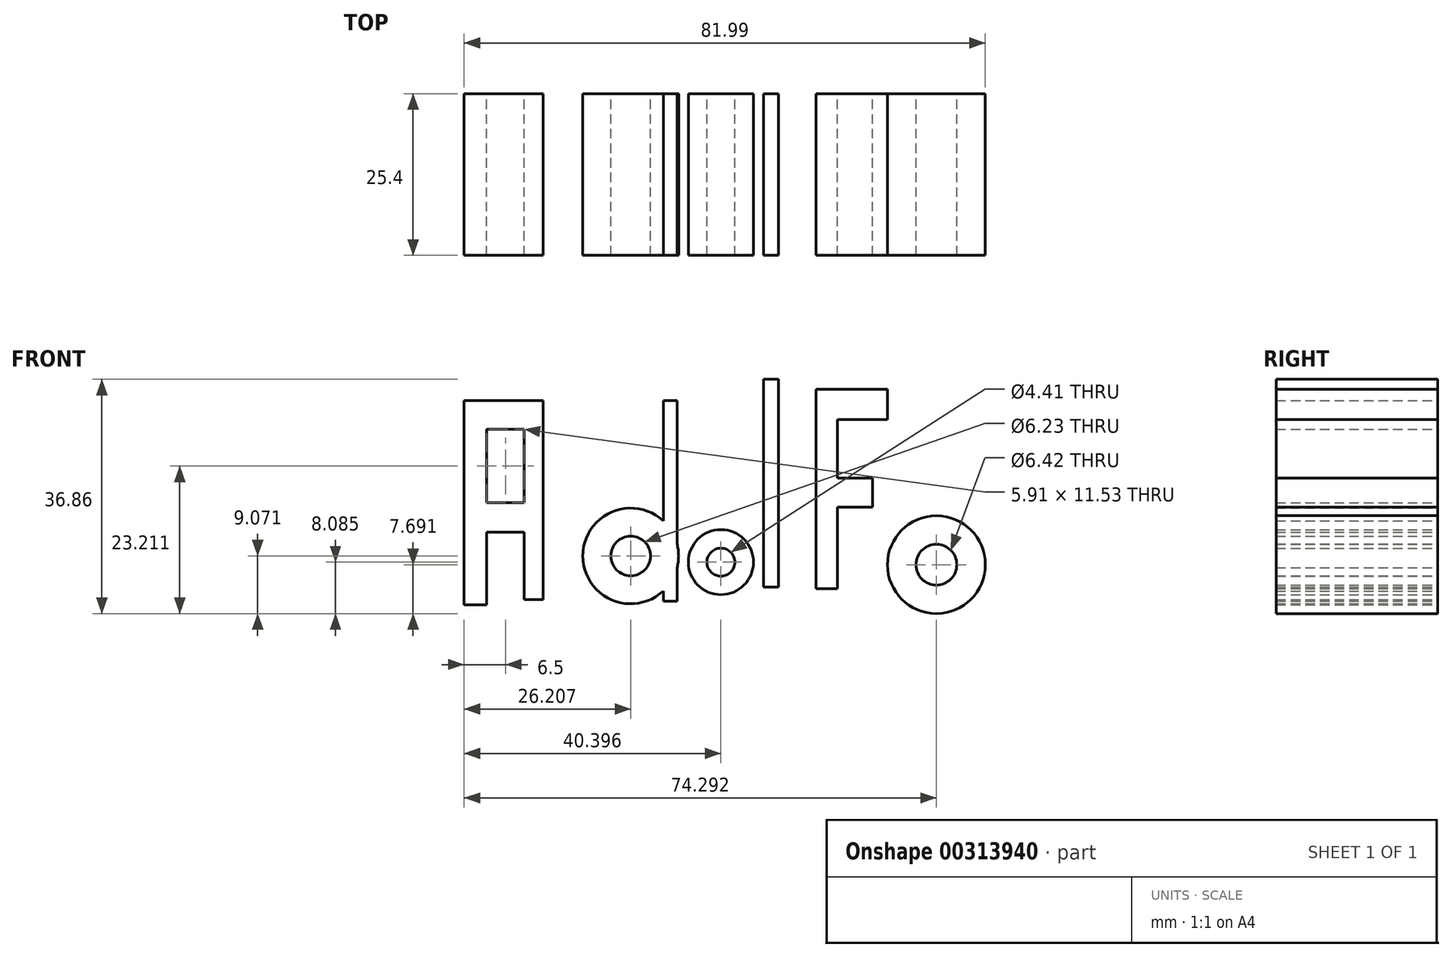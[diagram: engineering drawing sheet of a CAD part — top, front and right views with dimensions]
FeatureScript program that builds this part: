
annotation { "Feature Type Name" : "Feature", "Feature Type Description" : "" }
export const myFeature = defineFeature(function(context is Context, id is Id, definition is map)
    precondition{}
    {
        {
            var Q0;
            Q0=qCreatedBy(makeId("Front.planeOp"),FACE);
            var sketch = newSketch(context, id + "F0", { "sketchPlane" : qUnion([Q0])});
            skCircle(sketch, "E0", {"center": v(-45.52, 28.18) * mm, "radius": 7.53 * mm});
            skCircle(sketch, "E1", {"center": v(-31.33, 27.2) * mm, "radius": 5.12 * mm});
            skCircle(sketch, "E2", {"center": v(2.56, 26.8) * mm, "radius": 7.7 * mm});
            skLineSegment(sketch, "E3.bottom", {"start": v(-71.73, 20.5) * mm, "end": v(-68.19, 20.5) * mm});
            skLineSegment(sketch, "E3.top", {"start": v(-71.73, 52.62) * mm, "end": v(-68.19, 52.62) * mm});
            skLineSegment(sketch, "E3.left", {"start": v(-71.73, 20.5) * mm, "end": v(-71.73, 52.62) * mm});
            skLineSegment(sketch, "E3.right", {"start": v(-68.19, 20.5) * mm, "end": v(-68.19, 52.62) * mm});
            skLineSegment(sketch, "E4.bottom", {"start": v(-71.73, 52.62) * mm, "end": v(-59.32, 52.62) * mm});
            skLineSegment(sketch, "E4.top", {"start": v(-71.73, 48.08) * mm, "end": v(-59.32, 48.08) * mm});
            skLineSegment(sketch, "E4.left", {"start": v(-71.73, 52.62) * mm, "end": v(-71.73, 48.08) * mm});
            skLineSegment(sketch, "E4.right", {"start": v(-59.32, 52.62) * mm, "end": v(-59.32, 48.08) * mm});
            skLineSegment(sketch, "E5.bottom", {"start": v(-59.32, 52.62) * mm, "end": v(-62.27, 52.62) * mm});
            skLineSegment(sketch, "E5.top", {"start": v(-59.32, 21.28) * mm, "end": v(-62.27, 21.28) * mm});
            skLineSegment(sketch, "E5.left", {"start": v(-59.32, 52.62) * mm, "end": v(-59.32, 21.28) * mm});
            skLineSegment(sketch, "E5.right", {"start": v(-62.27, 52.62) * mm, "end": v(-62.27, 21.28) * mm});
            skLineSegment(sketch, "E6.bottom", {"start": v(-71.73, 36.56) * mm, "end": v(-59.32, 36.56) * mm});
            skLineSegment(sketch, "E6.top", {"start": v(-71.73, 31.93) * mm, "end": v(-59.32, 31.93) * mm});
            skLineSegment(sketch, "E6.left", {"start": v(-71.73, 36.56) * mm, "end": v(-71.73, 31.93) * mm});
            skLineSegment(sketch, "E6.right", {"start": v(-59.32, 36.56) * mm, "end": v(-59.32, 31.93) * mm});
            skLineSegment(sketch, "E7.bottom", {"start": v(-38.23, 21.09) * mm, "end": v(-40.4, 21.09) * mm});
            skLineSegment(sketch, "E7.top", {"start": v(-38.23, 52.62) * mm, "end": v(-40.4, 52.62) * mm});
            skLineSegment(sketch, "E7.left", {"start": v(-38.23, 21.09) * mm, "end": v(-38.23, 52.62) * mm});
            skLineSegment(sketch, "E7.right", {"start": v(-40.4, 21.09) * mm, "end": v(-40.4, 52.62) * mm});
            skLineSegment(sketch, "E8.bottom", {"start": v(-22.27, 23.25) * mm, "end": v(-24.63, 23.25) * mm});
            skLineSegment(sketch, "E8.top", {"start": v(-22.27, 55.97) * mm, "end": v(-24.63, 55.97) * mm});
            skLineSegment(sketch, "E8.left", {"start": v(-22.27, 23.25) * mm, "end": v(-22.27, 55.97) * mm});
            skLineSegment(sketch, "E8.right", {"start": v(-24.63, 23.25) * mm, "end": v(-24.63, 55.97) * mm});
            skLineSegment(sketch, "E9.bottom", {"start": v(-16.36, 54.4) * mm, "end": v(-13, 54.4) * mm});
            skLineSegment(sketch, "E9.top", {"start": v(-16.36, 23.06) * mm, "end": v(-13, 23.06) * mm});
            skLineSegment(sketch, "E9.left", {"start": v(-16.36, 54.4) * mm, "end": v(-16.36, 23.06) * mm});
            skLineSegment(sketch, "E9.right", {"start": v(-13, 54.4) * mm, "end": v(-13, 23.06) * mm});
            skLineSegment(sketch, "E10.bottom", {"start": v(-16.36, 54.4) * mm, "end": v(-5.12, 54.4) * mm});
            skLineSegment(sketch, "E10.top", {"start": v(-16.36, 49.66) * mm, "end": v(-5.12, 49.66) * mm});
            skLineSegment(sketch, "E10.left", {"start": v(-16.36, 54.4) * mm, "end": v(-16.36, 49.66) * mm});
            skLineSegment(sketch, "E10.right", {"start": v(-5.12, 54.4) * mm, "end": v(-5.12, 49.66) * mm});
            skLineSegment(sketch, "E11.bottom", {"start": v(-16.36, 40.4) * mm, "end": v(-7.49, 40.4) * mm});
            skLineSegment(sketch, "E11.top", {"start": v(-16.36, 35.87) * mm, "end": v(-7.49, 35.87) * mm});
            skLineSegment(sketch, "E11.left", {"start": v(-16.36, 40.4) * mm, "end": v(-16.36, 35.87) * mm});
            skLineSegment(sketch, "E11.right", {"start": v(-7.49, 40.4) * mm, "end": v(-7.49, 35.87) * mm});
            skPoint(sketch, "E12.oppositeSnap0", {"position": v(-65.53, 36.56) * mm});
            skLineSegment(sketch, "E12.bottom", {"start": v(-66.02, 43.95) * mm, "end": v(-65.53, 43.95) * mm});
            skLineSegment(sketch, "E12.top", {"start": v(-66.02, 39.41) * mm, "end": v(-65.53, 39.41) * mm});
            skLineSegment(sketch, "E12.left", {"start": v(-66.02, 43.95) * mm, "end": v(-66.02, 39.41) * mm});
            skLineSegment(sketch, "E12.right", {"start": v(-65.53, 43.95) * mm, "end": v(-65.53, 39.41) * mm});
            skCircle(sketch, "E13", {"center": v(-45.52, 28.18) * mm, "radius": 3.12 * mm});
            skCircle(sketch, "E14", {"center": v(-31.33, 27.2) * mm, "radius": 2.2 * mm});
            skCircle(sketch, "E15", {"center": v(2.56, 26.8) * mm, "radius": 3.2 * mm});
            skSolve(sketch);
        }
        {
            var Q0;
            Q0 = qSketchRegion(id + "F0", true);
            extrude(context, id + "F1", {"entities" : qUnion([Q0]), "depth" : 25.4 * mm});
        }
    });
